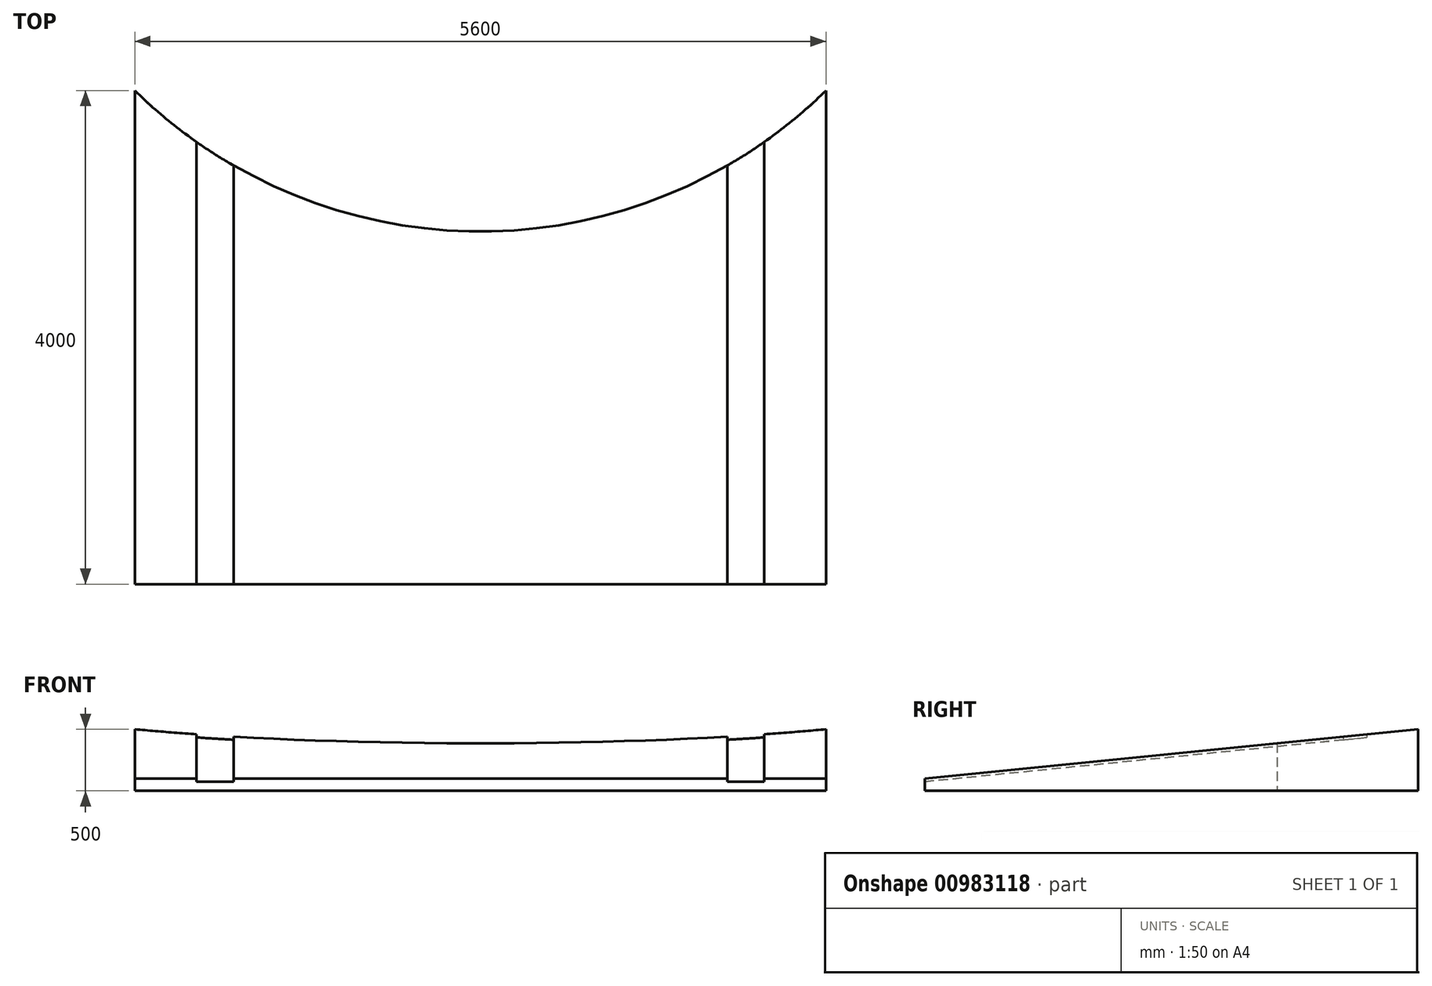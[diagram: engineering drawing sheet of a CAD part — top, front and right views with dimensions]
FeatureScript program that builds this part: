
annotation { "Feature Type Name" : "Feature", "Feature Type Description" : "" }
export const myFeature = defineFeature(function(context is Context, id is Id, definition is map)
    precondition{}
    {
        {
            var Q0;
            Q0=qCreatedBy(makeId("Right.planeOp"),FACE);
            var sketch = newSketch(context, id + "F0", { "sketchPlane" : qUnion([Q0])});
            skLineSegment(sketch, "E0", {"start": v(0, 0) * mm, "end": v(-4000, 0) * mm});
            skLineSegment(sketch, "E1", {"start": v(-4000, 0) * mm, "end": v(-4000, 100) * mm});
            skLineSegment(sketch, "E2", {"start": v(-4000, 100) * mm, "end": v(0, 500) * mm});
            skLineSegment(sketch, "E3", {"start": v(0, 500) * mm, "end": v(0, 0) * mm});
            skSolve(sketch);
        }
        {
            var Q0;
            Q0 = qSketchRegion(id + "F0", true);
            extrude(context, id + "F1", {"entities" : qUnion([Q0]), "endBound" : BoundingType.SYMMETRIC, "depth" : 5600 * mm, "offsetDistance" : 25 * mm});
        }
        {
            var Q0;
            Q0=qCreatedBy(makeId("Top.planeOp"),FACE);
            var sketch = newSketch(context, id + "F2", { "sketchPlane" : qUnion([Q0])});
            skCircle(sketch, "E4", {"center": v(0, 2856.57) * mm, "radius": 4000 * mm});
            skSolve(sketch);
        }
        {
            var Q0;
            Q0 = qSketchRegion(id + "F2", true);
            extrude(context, id + "F3", {"entities" : qUnion([Q0]), "operationType" : NewBodyOperationType.REMOVE, "depth" : 500 * mm, "offsetDistance" : 25 * mm});
        }
        {
            var Q0;
            Q0=makeQuery(id+"F1.opExtrude","SWEPT_FACE",FACE,{"disambiguationData":[OSD([sQuery(id+"F0.wireOp",EDGE,"E2")])]});
            var sketch = newSketch(context, id + "F4", { "sketchPlane" : qUnion([Q0])});
            skLineSegment(sketch, "E5", {"start": v(-2300, -4368.37) * mm, "end": v(-2300, -368.37) * mm});
            skLineSegment(sketch, "E6", {"start": v(-2300, -368.37) * mm, "end": v(-2000, -368.37) * mm});
            skLineSegment(sketch, "E7", {"start": v(-2000, -368.37) * mm, "end": v(-2000, -4368.37) * mm});
            skLineSegment(sketch, "E8", {"start": v(-2000, -4368.37) * mm, "end": v(-2300, -4368.37) * mm});
            skLineSegment(sketch, "E9.MirrorCS", {"start": v(2300, -4368.37) * mm, "end": v(2300, -368.37) * mm});
            skLineSegment(sketch, "E10.MirrorCS", {"start": v(2000, -368.37) * mm, "end": v(2000, -4368.37) * mm});
            skLineSegment(sketch, "E11.MirrorCS", {"start": v(2000, -4368.37) * mm, "end": v(2300, -4368.37) * mm});
            skLineSegment(sketch, "E12.MirrorCS", {"start": v(2300, -368.37) * mm, "end": v(2000, -368.37) * mm});
            skSolve(sketch);
        }
        {
            var Q0;
            Q0 = qSketchRegion(id + "F4", true);
            extrude(context, id + "F5", {"entities" : qUnion([Q0]), "operationType" : NewBodyOperationType.REMOVE, "oppositeDirection" : true, "depth" : 25 * mm, "offsetDistance" : 25 * mm});
        }
    });
